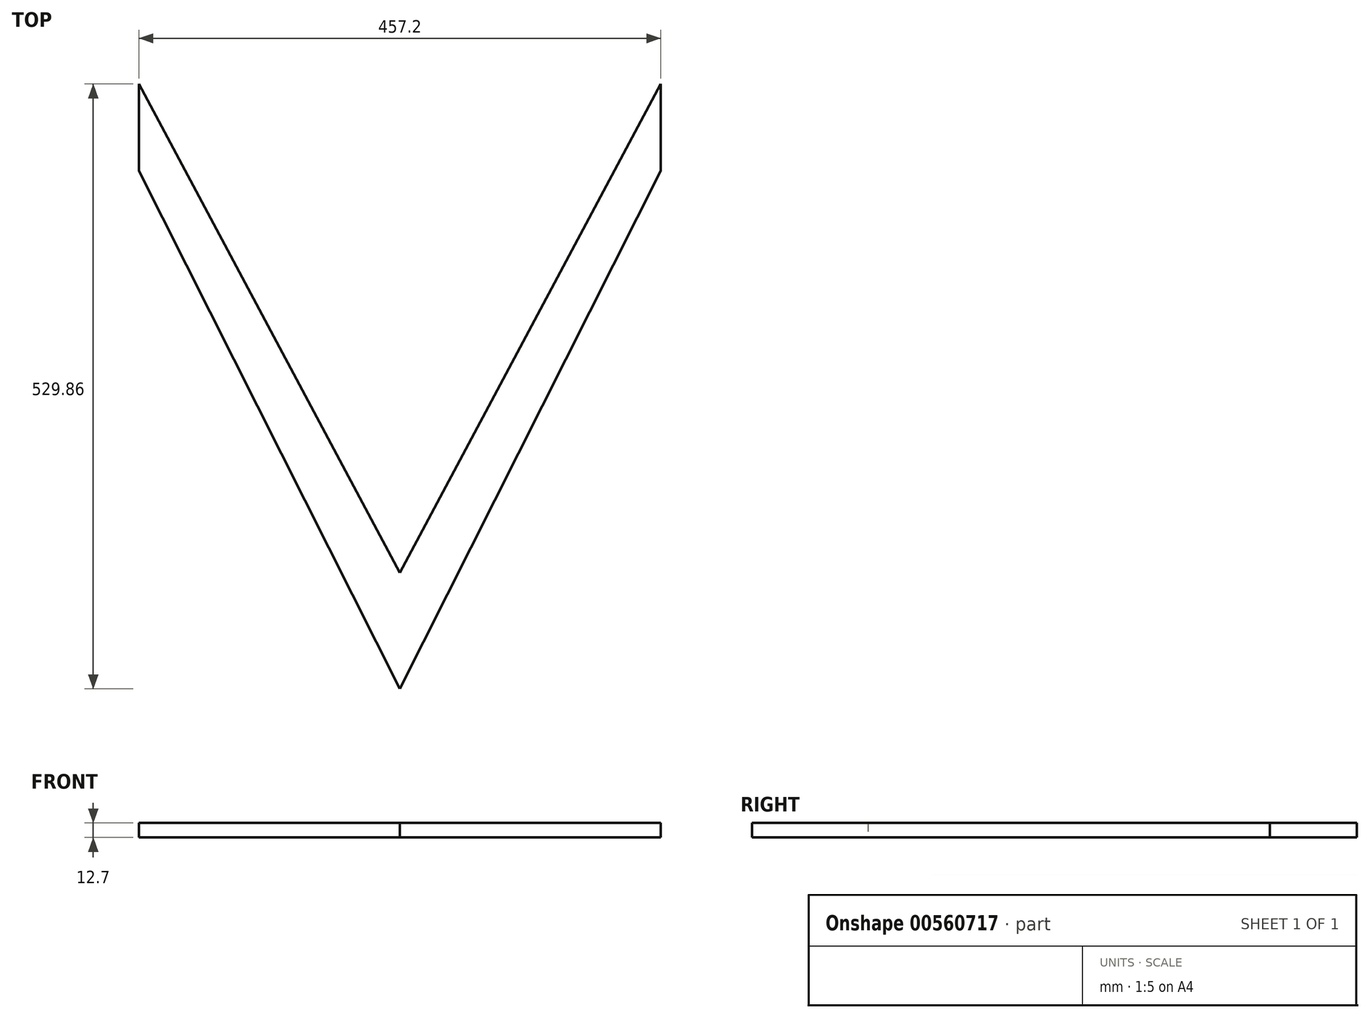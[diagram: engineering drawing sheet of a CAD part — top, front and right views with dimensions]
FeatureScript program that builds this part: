
annotation { "Feature Type Name" : "Feature", "Feature Type Description" : "" }
export const myFeature = defineFeature(function(context is Context, id is Id, definition is map)
    precondition{}
    {
        {
            var Q0;
            Q0=qCreatedBy(makeId("Top.planeOp"),FACE);
            var sketch = newSketch(context, id + "F0", { "sketchPlane" : qUnion([Q0])});
            skLineSegment(sketch, "E0", {"start": v(0, 50.06) * mm, "end": v(-228.6, 50.06) * mm});
            skLineSegment(sketch, "E1", {"start": v(0, 50.06) * mm, "end": v(0, -102.34) * mm});
            skSolve(sketch);
        }
        {
            var Q0;
            Q0=qCreatedBy(makeId("Top.planeOp"),FACE);
            var sketch = newSketch(context, id + "F1", { "sketchPlane" : qUnion([Q0])});
            skLineSegment(sketch, "E2", {"start": v(0, -101.6) * mm, "end": v(-228.6, 352.06) * mm});
            skLineSegment(sketch, "E3", {"start": v(-228.6, 352.06) * mm, "end": v(-228.6, 428.26) * mm});
            skLineSegment(sketch, "E4", {"start": v(-228.6, 428.26) * mm, "end": v(0, 0) * mm});
            skLineSegment(sketch, "E5.MirrorCS", {"start": v(228.6, 428.26) * mm, "end": v(0, 0) * mm});
            skLineSegment(sketch, "E6.MirrorCS", {"start": v(0, -101.6) * mm, "end": v(228.6, 352.06) * mm});
            skLineSegment(sketch, "E7.MirrorCS", {"start": v(228.6, 352.06) * mm, "end": v(228.6, 428.26) * mm});
            skLineSegment(sketch, "E8", {"start": v(0, 0) * mm, "end": v(0, -101.6) * mm});
            skSolve(sketch);
        }
        {
            var Q0;
            Q0=makeQuery(id+"F1.imprint","IMPRINT",FACE,{"disambiguationData":[TD([[makeQuery(id+"F1.imprint","IMPRINT",EDGE,{"derivedFrom":sQuery(id+"F1.wireOp",EDGE,"E2")}),-1.0]])]});
            var Q1;
            Q1=makeQuery(id+"F1.imprint","IMPRINT",FACE,{"disambiguationData":[TD([[makeQuery(id+"F1.imprint","IMPRINT",EDGE,{"derivedFrom":sQuery(id+"F1.wireOp",EDGE,"E5.MirrorCS")}),1.0]])]});
            extrude(context, id + "F2", {"entities" : qUnion([Q0, Q1]), "depth" : 12.7 * mm, "offsetDistance" : 25.4 * mm});
        }
    });
